annotation { "Feature Type Name" : "Feature", "Feature Type Description" : "" }
export const myFeature = defineFeature(function(context is Context, id is Id, definition is map)
    precondition{}
    {
        {
            var Q0;
            Q0=qCreatedBy(makeId("Top.planeOp"),FACE);
            var sketch = newSketch(context, id + "F0", { "sketchPlane" : qUnion([Q0])});
            skLineSegment(sketch, "E0.bottom", {"start": v(-72.48, -16.73) * mm, "end": v(79.92, -16.73) * mm, "construction": true});
            skLineSegment(sketch, "E0.top", {"start": v(-72.48, -42.13) * mm, "end": v(79.92, -42.13) * mm, "construction": true});
            skLineSegment(sketch, "E0.left", {"start": v(-72.48, -16.73) * mm, "end": v(-72.48, -42.13) * mm, "construction": true});
            skLineSegment(sketch, "E0.right", {"start": v(79.92, -16.73) * mm, "end": v(79.92, -42.13) * mm, "construction": true});
            skText(sketch, "E1", { "text": "FAA ESU", "fontName": "OpenSans-Regular.ttf"});
            skLineSegment(sketch, "E2", {"start": v(-41.25, -25.6) * mm, "end": v(-38.75, -24.86) * mm});
            skLineSegment(sketch, "E3", {"start": v(-40.85, -26.64) * mm, "end": v(-38.3, -25.9) * mm});
            skLineSegment(sketch, "E4", {"start": v(-45.3, -26.45) * mm, "end": v(-48.58, -27.8) * mm});
            skLineSegment(sketch, "E5", {"start": v(-45.98, -28.18) * mm, "end": v(-49.4, -29.59) * mm});
            const initialGuessF0  = {"E1": [-0.07248, -0.04213, 1, 0, 0.0254]};
            skSetInitialGuess(sketch, initialGuessF0);
            skSolve(sketch);
        }
        {
            var Q0;
            Q0=qCreatedBy(makeId("Top.planeOp"),FACE);
            var sketch = newSketch(context, id + "F1", { "sketchPlane" : qUnion([Q0])});
            skLineSegment(sketch, "E6.bottom", {"start": v(-95.1, 9.47) * mm, "end": v(108.1, 9.47) * mm});
            skLineSegment(sketch, "E6.top", {"start": v(-95.1, -66.73) * mm, "end": v(108.1, -66.73) * mm});
            skLineSegment(sketch, "E6.left", {"start": v(-95.1, 9.47) * mm, "end": v(-95.1, -66.73) * mm});
            skLineSegment(sketch, "E6.right", {"start": v(108.1, 9.47) * mm, "end": v(108.1, -66.73) * mm});
            skSolve(sketch);
        }
        {
            var Q0;
            Q0 = qSketchRegion(id + "F1", true);
            extrude(context, id + "F2", {"entities" : qUnion([Q0]), "depth" : 1 * mm, "offsetDistance" : 25.4 * mm});
        }
        {
            var Q0;
            Q0 = qSketchRegion(id + "F0", true);
            extrude(context, id + "F3", {"entities" : qUnion([Q0]), "operationType" : NewBodyOperationType.REMOVE, "depth" : 26.16 * mm, "offsetDistance" : 25.4 * mm});
        }
        {
            var Q0;
            Q0=makeQuery(id+"F3.boolean.opBoolean","COPY",FACE,{"derivedFrom":makeQuery(id+"F3.opExtrude","SWEPT_FACE",FACE,{"disambiguationData":[OSD([sQuery(id+"F0.wireOp",EDGE,"E1.sketch_text.stroke-18")])]})});
            var sketch = newSketch(context, id + "F4", { "sketchPlane" : qUnion([Q0])});
            skLineSegment(sketch, "E7.bottom", {"start": v(-8.53, 1) * mm, "end": v(-9.6, 1) * mm});
            skLineSegment(sketch, "E7.top", {"start": v(-8.53, 0) * mm, "end": v(-9.6, 0) * mm});
            skLineSegment(sketch, "E7.left", {"start": v(-8.53, 1) * mm, "end": v(-8.53, 0) * mm});
            skLineSegment(sketch, "E7.right", {"start": v(-9.6, 1) * mm, "end": v(-9.6, 0) * mm});
            skSolve(sketch);
        }
        {
            var Q0;
            Q0=makeQuery(id+"F4.imprint","IMPRINT",FACE,{"disambiguationData":[TD([[makeQuery(id+"F4.imprint","IMPRINT",EDGE,{"derivedFrom":sQuery(id+"F4.wireOp",EDGE,"E7.bottom")}),1.0]])]});
            extrude(context, id + "F5", {"entities" : qUnion([Q0]), "endBound" : BoundingType.SYMMETRIC, "depth" : 20.93 * mm, "offsetDistance" : 25.4 * mm});
        }
        {
            var Q0;
            Q0=makeQuery(id+"F3.boolean.opBoolean","COPY",FACE,{"derivedFrom":makeQuery(id+"F3.opExtrude","SWEPT_FACE",FACE,{"disambiguationData":[OSD([sQuery(id+"F0.wireOp",EDGE,"E1.sketch_text.stroke-31")])]})});
            var sketch = newSketch(context, id + "F6", { "sketchPlane" : qUnion([Q0])});
            skLineSegment(sketch, "E8.bottom", {"start": v(-17.2, 1) * mm, "end": v(-18.48, 1) * mm});
            skLineSegment(sketch, "E8.top", {"start": v(-17.2, 0) * mm, "end": v(-18.48, 0) * mm});
            skLineSegment(sketch, "E8.left", {"start": v(-17.2, 1) * mm, "end": v(-17.2, 0) * mm});
            skLineSegment(sketch, "E8.right", {"start": v(-18.48, 1) * mm, "end": v(-18.48, 0) * mm});
            skSolve(sketch);
        }
        {
            var Q0;
            Q0=makeQuery(id+"F6.imprint","IMPRINT",FACE,{"disambiguationData":[TD([[makeQuery(id+"F6.imprint","IMPRINT",EDGE,{"derivedFrom":sQuery(id+"F6.wireOp",EDGE,"E8.bottom")}),1.0]])]});
            extrude(context, id + "F7", {"entities" : qUnion([Q0]), "endBound" : BoundingType.SYMMETRIC, "depth" : 25.4 * mm, "offsetDistance" : 25.4 * mm});
        }
    });